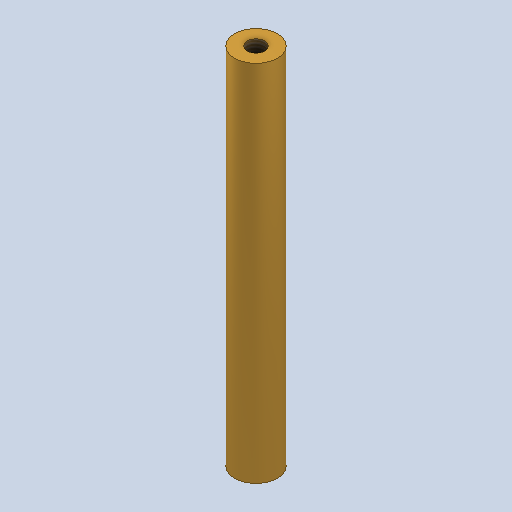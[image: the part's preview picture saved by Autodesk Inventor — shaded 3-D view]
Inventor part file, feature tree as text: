
AUTODESK INVENTOR PART (.ipt)
format: ipt  version: 2023 (Build 270158000, 158)  size: 254,464 bytes
history: native  units: mm
features: sketch x3, hole x2, other x1, extrude x1
ambient origin geometry x8: Origin, YZ Plane, XZ Plane, XY Plane, X Axis, Y Axis, Z Axis, Center Point
bodies: Body1 (feature_tree)
feature tree (7):
  other  "Sólido1"
  extrude  "Extrusão1"  Depth=85.0mm TaperAngle=0.0deg
  hole  "Furo1"  [1 undecoded]
  hole  "Furo2"  [1 undecoded]
  sketch  "Esboço1"  dims[d1=10.0mm d2=85.0mm d3=0.0mm]
  sketch  "Esboço2"  dims[d4=4.134mm d5=10.0mm d6=4.0mm d7=2.0mm d8=90.0deg d9=14.2mm d10=20.594885mm]
  sketch  "Esboço3"  dims[d11=4.134mm d12=10.0mm d13=4.0mm d14=2.0mm d15=90.0deg d16=14.2mm d17=20.594885mm]
note: 2 required parameter values undecoded (feature->parameter linkage not recoverable at this tier; creation-order binding heuristic only, values carry confidence <= 0.55)
